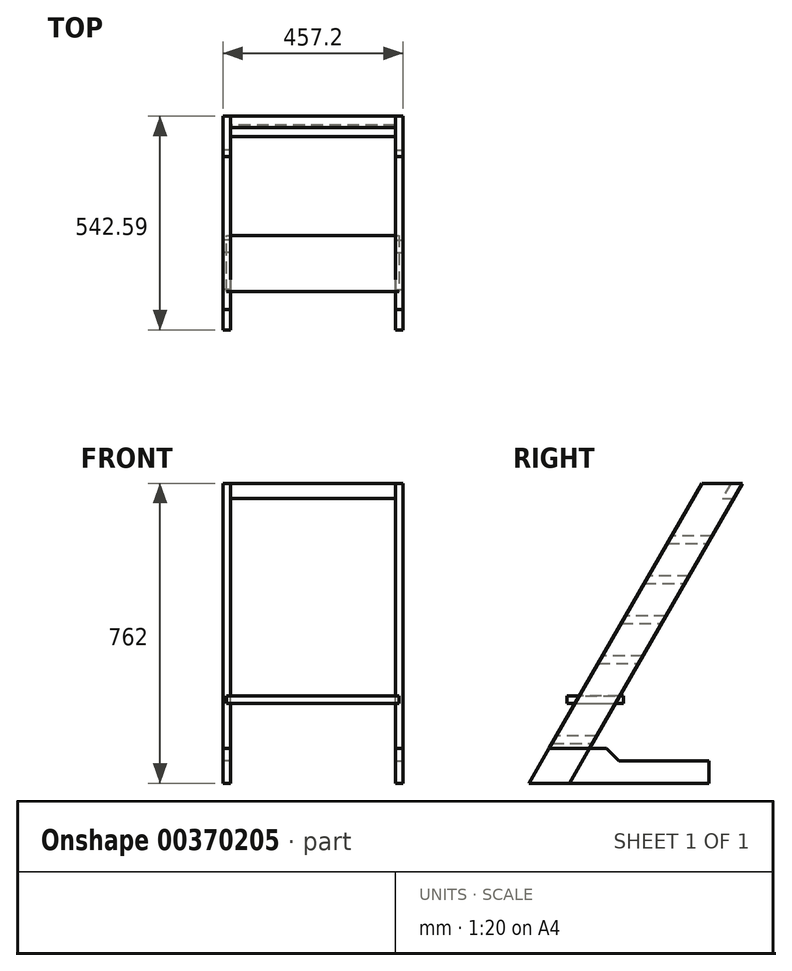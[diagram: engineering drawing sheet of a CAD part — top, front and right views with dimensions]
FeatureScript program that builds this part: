
annotation { "Feature Type Name" : "Feature", "Feature Type Description" : "" }
export const myFeature = defineFeature(function(context is Context, id is Id, definition is map)
    precondition{}
    {
        {
            var Q0;
            Q0=qCreatedBy(makeId("Right.planeOp"),FACE);
            var sketch = newSketch(context, id + "F0", { "sketchPlane" : qUnion([Q0])});
            skLineSegment(sketch, "E0", {"start": v(0, 0) * mm, "end": v(439.94, 762) * mm});
            skLineSegment(sketch, "E1", {"start": v(439.94, 762) * mm, "end": v(542.6, 762) * mm});
            skLineSegment(sketch, "E2", {"start": v(542.6, 762) * mm, "end": v(102.65, 0) * mm});
            skLineSegment(sketch, "E3", {"start": v(102.65, 0) * mm, "end": v(0, 0) * mm});
            skSolve(sketch);
        }
        {
            var Q0;
            Q0=makeQuery(id+"F0.imprint","IMPRINT",FACE,{"disambiguationData":[TD([[makeQuery(id+"F0.imprint","IMPRINT",EDGE,{"derivedFrom":sQuery(id+"F0.wireOp",EDGE,"E0")}),-1.0]])]});
            extrude(context, id + "F1", {"entities" : qUnion([Q0]), "depth" : 19.05 * mm});
        }
        {
            var Q0;
            Q0=makeQuery(id+"F1.opExtrude","CAP_FACE",FACE,{"disambiguationData":[OSD([sQuery(id+"F0.wireOp",EDGE,"E0"),sQuery(id+"F0.wireOp",EDGE,"E1"),sQuery(id+"F0.wireOp",EDGE,"E2"),sQuery(id+"F0.wireOp",EDGE,"E3")])],"isStart":false});
            var sketch = newSketch(context, id + "F2", { "sketchPlane" : qUnion([Q0])});
            skLineSegment(sketch, "E4", {"start": v(0, 0) * mm, "end": v(102.65, 0) * mm});
            skLineSegment(sketch, "E5", {"start": v(102.65, 0) * mm, "end": v(153.98, 88.9) * mm});
            skLineSegment(sketch, "E6", {"start": v(153.98, 88.9) * mm, "end": v(51.33, 88.9) * mm});
            skLineSegment(sketch, "E7", {"start": v(51.33, 88.9) * mm, "end": v(0, 0) * mm});
            skSolve(sketch);
        }
        {
            var Q0;
            Q0=makeQuery(id+"F2.imprint","IMPRINT",FACE,{"disambiguationData":[TD([[makeQuery(id+"F2.imprint","IMPRINT",EDGE,{"derivedFrom":sQuery(id+"F2.wireOp",EDGE,"E4")}),-1.0]])]});
            extrude(context, id + "F3", {"entities" : qUnion([Q0]), "operationType" : NewBodyOperationType.REMOVE, "oppositeDirection" : true, "depth" : .75 / 50.8 * mm});
        }
        {
            var Q0;
            Q0=qCreatedBy(makeId("Right.planeOp"),FACE);
            var sketch = newSketch(context, id + "F4", { "sketchPlane" : qUnion([Q0])});
            skLineSegment(sketch, "E8", {"start": v(0, 0) * mm, "end": v(457.2, 0) * mm});
            skLineSegment(sketch, "E9", {"start": v(457.2, 0) * mm, "end": v(457.2, 57.15) * mm});
            skLineSegment(sketch, "E10", {"start": v(196.85, 88.9) * mm, "end": v(51.33, 88.9) * mm});
            skLineSegment(sketch, "E11", {"start": v(51.33, 88.9) * mm, "end": v(0, 0) * mm});
            skLineSegment(sketch, "E12", {"start": v(457.2, 57.15) * mm, "end": v(228.6, 57.15) * mm});
            skLineSegment(sketch, "E13", {"start": v(228.6, 57.15) * mm, "end": v(196.85, 88.9) * mm});
            skSolve(sketch);
        }
        {
            var Q0;
            Q0 = qSketchRegion(id + "F4", true);
            extrude(context, id + "F5", {"entities" : qUnion([Q0]), "depth" : 19.05 * mm});
        }
        {
            var Q0;
            Q0=makeQuery(id+"F5.opExtrude","CAP_FACE",FACE,{"disambiguationData":[OSD([sQuery(id+"F4.wireOp",EDGE,"E8"),sQuery(id+"F4.wireOp",EDGE,"E9"),sQuery(id+"F4.wireOp",EDGE,"E10"),sQuery(id+"F4.wireOp",EDGE,"E11")])],"isStart":true});
            var sketch = newSketch(context, id + "F6", { "sketchPlane" : qUnion([Q0])});
            skLineSegment(sketch, "E14", {"start": v(-51.33, 88.9) * mm, "end": v(-153.98, 88.9) * mm});
            skLineSegment(sketch, "E15", {"start": v(-153.98, 88.9) * mm, "end": v(-102.65, 0) * mm});
            skLineSegment(sketch, "E16", {"start": v(-102.65, 0) * mm, "end": v(0, 0) * mm});
            skLineSegment(sketch, "E17", {"start": v(0, 0) * mm, "end": v(-51.33, 88.9) * mm});
            skSolve(sketch);
        }
        {
            var Q0;
            Q0=makeQuery(id+"F6.imprint","IMPRINT",FACE,{"disambiguationData":[TD([[makeQuery(id+"F6.imprint","IMPRINT",EDGE,{"derivedFrom":sQuery(id+"F6.wireOp",EDGE,"E14")}),-1.0]])]});
            extrude(context, id + "F7", {"entities" : qUnion([Q0]), "operationType" : NewBodyOperationType.REMOVE, "oppositeDirection" : true, "depth" : .75 / 50.8 * mm});
        }
        {
            var Q0;
            Q0=makeQuery(id+"F1.opExtrude","CAP_FACE",FACE,{"disambiguationData":[OSD([sQuery(id+"F0.wireOp",EDGE,"E0"),sQuery(id+"F0.wireOp",EDGE,"E1"),sQuery(id+"F0.wireOp",EDGE,"E2"),sQuery(id+"F0.wireOp",EDGE,"E3")])],"isStart":false});
            var sketch = newSketch(context, id + "F8", { "sketchPlane" : qUnion([Q0])});
            skLineSegment(sketch, "E18", {"start": v(0, 101.6) * mm, "end": v(542.6, 101.6) * mm});
            skLineSegment(sketch, "E19", {"start": v(542.6, 101.6) * mm, "end": v(542.6, 120.65) * mm});
            skLineSegment(sketch, "E20", {"start": v(542.6, 120.65) * mm, "end": v(0, 120.65) * mm});
            skLineSegment(sketch, "E21", {"start": v(0, 120.65) * mm, "end": v(0, 101.6) * mm});
            skLineSegment(sketch, "E22.0.1.0", {"start": v(542.6, 222.25) * mm, "end": v(0, 222.25) * mm});
            skLineSegment(sketch, "E22.0.1.1", {"start": v(0, 203.2) * mm, "end": v(542.6, 203.2) * mm});
            skLineSegment(sketch, "E22.0.1.2", {"start": v(542.6, 203.2) * mm, "end": v(542.6, 222.25) * mm});
            skLineSegment(sketch, "E22.0.1.3", {"start": v(0, 222.25) * mm, "end": v(0, 203.2) * mm});
            skLineSegment(sketch, "E22.0.2.0", {"start": v(542.6, 323.85) * mm, "end": v(0, 323.85) * mm});
            skLineSegment(sketch, "E22.0.2.1", {"start": v(0, 304.8) * mm, "end": v(542.6, 304.8) * mm});
            skLineSegment(sketch, "E22.0.2.2", {"start": v(542.6, 304.8) * mm, "end": v(542.6, 323.85) * mm});
            skLineSegment(sketch, "E22.0.2.3", {"start": v(0, 323.85) * mm, "end": v(0, 304.8) * mm});
            skLineSegment(sketch, "E22.0.3.0", {"start": v(542.6, 425.45) * mm, "end": v(0, 425.45) * mm});
            skLineSegment(sketch, "E22.0.3.1", {"start": v(0, 406.4) * mm, "end": v(542.6, 406.4) * mm});
            skLineSegment(sketch, "E22.0.3.2", {"start": v(542.6, 406.4) * mm, "end": v(542.6, 425.45) * mm});
            skLineSegment(sketch, "E22.0.3.3", {"start": v(0, 425.45) * mm, "end": v(0, 406.4) * mm});
            skLineSegment(sketch, "E22.0.4.0", {"start": v(542.6, 527.05) * mm, "end": v(0, 527.05) * mm});
            skLineSegment(sketch, "E22.0.4.1", {"start": v(0, 508) * mm, "end": v(542.6, 508) * mm});
            skLineSegment(sketch, "E22.0.4.2", {"start": v(542.6, 508) * mm, "end": v(542.6, 527.05) * mm});
            skLineSegment(sketch, "E22.0.4.3", {"start": v(0, 527.05) * mm, "end": v(0, 508) * mm});
            skLineSegment(sketch, "E22.direction1", {"start": v(0, 101.6) * mm, "end": v(25.4, 101.6) * mm, "construction": true});
            skLineSegment(sketch, "E22.direction2", {"start": v(0, 101.6) * mm, "end": v(0, 203.2) * mm, "construction": true});
            skLineSegment(sketch, "E23.0.0.5", {"start": v(542.6, 628.65) * mm, "end": v(0, 628.65) * mm});
            skLineSegment(sketch, "E23.3.0.5", {"start": v(0, 609.6) * mm, "end": v(542.6, 609.6) * mm});
            skLineSegment(sketch, "E23.6.0.5", {"start": v(542.6, 609.6) * mm, "end": v(542.6, 628.65) * mm});
            skLineSegment(sketch, "E23.9.0.5", {"start": v(0, 628.65) * mm, "end": v(0, 609.6) * mm});
            skSolve(sketch);
        }
        {
            var Q0;
            Q0 = qSketchRegion(id + "F8", true);
            extrude(context, id + "F9", {"entities" : qUnion([Q0]), "operationType" : NewBodyOperationType.REMOVE, "oppositeDirection" : true, "depth" : .75 / 50.8 * mm});
        }
        {
            var Q0;
            Q0=qCreatedBy(makeId("Right.planeOp"),FACE);
            cPlane(context, id + "F10", {"entities" : qUnion([Q0]), "cplaneType" : CPlaneType.OFFSET, "offset" : 228.6 * mm, "width" : 152.4 * mm, "height" : 152.4 * mm});
        }
        {
            var Q0;
            Q0=makeQuery(id+"F1.opExtrude","SWEPT_BODY",BODY,{"disambiguationData":[OSD([sQuery(id+"F0.wireOp",EDGE,"E0"),sQuery(id+"F0.wireOp",EDGE,"E1"),sQuery(id+"F0.wireOp",EDGE,"E2"),sQuery(id+"F0.wireOp",EDGE,"E3")])]});
            var Q1;
            Q1=makeQuery(id+"F5.opExtrude","SWEPT_BODY",BODY,{"disambiguationData":[OSD([sQuery(id+"F4.wireOp",EDGE,"E8"),sQuery(id+"F4.wireOp",EDGE,"E9"),sQuery(id+"F4.wireOp",EDGE,"E10"),sQuery(id+"F4.wireOp",EDGE,"E11")])]});
            var Q2;
            Q2=qCreatedBy(id+"F10.planeOp",FACE);
            mirror(context, id + "F11", {"entities" : qUnion([Q0, Q1]), "mirrorPlane" : qUnion([Q2])});
        }
        {
            var Q0;
            Q0=makeQuery(id+"F9.boolean.opBoolean","COPY",FACE,{"derivedFrom":makeQuery(id+"F9.opExtrude","SWEPT_FACE",FACE,{"disambiguationData":[OSD([sQuery(id+"F8.wireOp",EDGE,"E22.0.1.1")])]})});
            var sketch = newSketch(context, id + "F12", { "sketchPlane" : qUnion([Q0])});
            skLineSegment(sketch, "E24", {"start": v(9.53, 97.2) * mm, "end": v(9.53, 240.08) * mm});
            skLineSegment(sketch, "E25", {"start": v(9.52, 240.08) * mm, "end": v(447.68, 240.08) * mm});
            skLineSegment(sketch, "E26", {"start": v(447.68, 240.08) * mm, "end": v(447.68, 97.2) * mm});
            skLineSegment(sketch, "E27", {"start": v(447.68, 97.2) * mm, "end": v(9.53, 97.2) * mm});
            skPoint(sketch, "E28", {"position": v(9.53, 168.64) * mm});
            skSolve(sketch);
        }
        {
            var Q0;
            Q0 = qSketchRegion(id + "F12", true);
            extrude(context, id + "F13", {"entities" : qUnion([Q0]), "depth" : 19.05 * mm});
        }
        {
            var Q0;
            {var subQ0=sQuery(id+"F0.wireOp",EDGE,"E0");var subQ1=sQuery(id+"F0.wireOp",EDGE,"E1");var subQ2=sQuery(id+"F0.wireOp",EDGE,"E2");Q0=makeQuery(id+"F9.boolean.opBoolean","SPLIT",FACE,{"disambiguationData":[TD([makeQuery(id+"F1.opExtrude","SWEPT_FACE",FACE,{"disambiguationData":[OSD([subQ1])]})])],"derivedFrom":makeQuery(id+"F1.opExtrude","CAP_FACE",FACE,{"disambiguationData":[OSD([subQ0,subQ1,subQ2,sQuery(id+"F0.wireOp",EDGE,"E3")])],"isStart":false})});}
            var sketch = newSketch(context, id + "F14", { "sketchPlane" : qUnion([Q0])});
            skLineSegment(sketch, "E29", {"start": v(542.6, 762) * mm, "end": v(520.6, 723.9) * mm});
            skLineSegment(sketch, "E30", {"start": v(520.6, 723.9) * mm, "end": v(491.27, 723.9) * mm});
            skLineSegment(sketch, "E31", {"start": v(491.27, 723.9) * mm, "end": v(513.26, 762) * mm});
            skLineSegment(sketch, "E32", {"start": v(513.26, 762) * mm, "end": v(542.6, 762) * mm});
            skSolve(sketch);
        }
        {
            var Q0;
            Q0=makeQuery(id+"F14.imprint","IMPRINT",FACE,{"disambiguationData":[TD([[makeQuery(id+"F14.imprint","IMPRINT",EDGE,{"derivedFrom":sQuery(id+"F14.wireOp",EDGE,"E29")}),-1.0]])]});
            extrude(context, id + "F15", {"entities" : qUnion([Q0]), "endBound" : BoundingType.UP_TO_NEXT, "depth" : 25.4 * mm});
        }
    });
